# Revit family: HPLC_BARCELONA
name_source: partatom
category: Furniture
units: mm (PartAtom-declared; Revit-internal decimal feet)

## family parameters
Always vertical = Yes
Cut with Voids When Loaded = No
OmniClass Number = 23.40.20.00
OmniClass Title = General Furniture and Specialties
Room Calculation Point = No
Shared = No
Work Plane-Based = No

## types (32) — shared parameters
BS = No
BS-15 = No
BS-9 = No
BSP-15 = No
BSP-9 = No
BS_PASSTHROUGH = No
CER = No
CUTOUT_CENTER = No
CUTOUT_CENTER_CHECK = No
CUTOUT_SIDES = No
CUTOUT_SIDES_CHECK = No
FIXED = Yes
FX_MARINE_EDGE = No
HA = No
HA_MARINE_EDGE = No
LOW_TAG = Yes
MARINE_EDGE = No
Manufacturer = IBR Innovasystem
SH1-12 = No
SH1-15 = No
SH1-9 = No
SH2-12 = No
SH2-15 = No
SH2-9 = No
SHELF_LEVEL_1 = No
SHELF_LEVEL_2 = No
URL = https://ibr-innovasystem.com
WT_MATERIAL = Plástico, blanco opaco
WT_THICK = 16 mm  [stored 0.0524934 ft]
zero-valued in all types: Cost, Default Elevation

## per-type parameters (varying)
| type | COLUMN_H | Depth | Description | Length | WTheight_nominal | WTheight_real |
| HPLCB-1575718 | 1800 mm  [stored 5.90551 ft] | 750 mm  [stored 2.46063 ft] | HPLC Bench Barcelona 1500x750x750/1800, 8xElectrical Outlets (Type TBD per project) | 1500 mm  [stored 4.92126 ft] | 750 mm  [stored 2.46063 ft] | 734 mm  [stored 2.40814 ft] |
| HPLCB-1575716 | 1570 mm | 750 mm  [stored 2.46063 ft] | HPLC Bench Barcelona 1500x750x750/1570, 8xElectrical Outlets (Type TBD per project) | 1500 mm  [stored 4.92126 ft] | 750 mm  [stored 2.46063 ft] | 734 mm  [stored 2.40814 ft] |
| HPLCB-1275718 | 1800 mm  [stored 5.90551 ft] | 750 mm  [stored 2.46063 ft] | HPLC Bench Barcelona 1200x750x750/1800, 8xElectrical Outlets (Type TBD per project) | 1200 mm  [stored 3.93701 ft] | 750 mm  [stored 2.46063 ft] | 734 mm  [stored 2.40814 ft] |
| HPLCB-1275716 | 1570 mm | 750 mm  [stored 2.46063 ft] | HPLC Bench Barcelona 1200x750x750/1570, 8xElectrical Outlets (Type TBD per project) | 1200 mm  [stored 3.93701 ft] | 750 mm  [stored 2.46063 ft] | 734 mm  [stored 2.40814 ft] |
| HPLCB-0975716 | 1570 mm | 750 mm  [stored 2.46063 ft] | HPLC Bench Barcelona 900x750x750/1570, 8xElectrical Outlets (Type TBD per project) | 900 mm  [stored 2.95276 ft] | 750 mm  [stored 2.46063 ft] | 734 mm  [stored 2.40814 ft] |
| HPLCB-0975718 | 1800 mm  [stored 5.90551 ft] | 750 mm  [stored 2.46063 ft] | HPLC Bench Barcelona 900x750x750/1800, 8xElectrical Outlets (Type TBD per project) | 900 mm  [stored 2.95276 ft] | 750 mm  [stored 2.46063 ft] | 734 mm  [stored 2.40814 ft] |
| HPLCB-7575718 | 1800 mm  [stored 5.90551 ft] | 750 mm  [stored 2.46063 ft] | HPLC Bench Barcelona 750x750x750/1800, 8xElectrical Outlets (Type TBD per project) | 750 mm  [stored 2.46063 ft] | 750 mm  [stored 2.46063 ft] | 734 mm  [stored 2.40814 ft] |
| HPLCB-7575716 | 1570 mm | 750 mm  [stored 2.46063 ft] | HPLC Bench Barcelona 750x750x750/1570, 8xElectrical Outlets (Type TBD per project) | 750 mm  [stored 2.46063 ft] | 750 mm  [stored 2.46063 ft] | 734 mm  [stored 2.40814 ft] |
| HPLCB-1590718 | 1800 mm  [stored 5.90551 ft] | 900 mm  [stored 2.95276 ft] | HPLC Bench Barcelona 1500x900x750/1800, 8xElectrical Outlets (Type TBD per project) | 1500 mm  [stored 4.92126 ft] | 750 mm  [stored 2.46063 ft] | 734 mm  [stored 2.40814 ft] |
| HPLCB-1590716 | 1570 mm | 900 mm  [stored 2.95276 ft] | HPLC Bench Barcelona 1500x900x750/1570, 8xElectrical Outlets (Type TBD per project) | 1500 mm  [stored 4.92126 ft] | 750 mm  [stored 2.46063 ft] | 734 mm  [stored 2.40814 ft] |
| HPLCB-1290716 | 1570 mm | 900 mm  [stored 2.95276 ft] | HPLC Bench Barcelona 1200x900x750/1570, 8xElectrical Outlets (Type TBD per project) | 1200 mm  [stored 3.93701 ft] | 750 mm  [stored 2.46063 ft] | 734 mm  [stored 2.40814 ft] |
| HPLCB-1290718 | 1800 mm  [stored 5.90551 ft] | 900 mm  [stored 2.95276 ft] | HPLC Bench Barcelona 1200x900x750/1800, 8xElectrical Outlets (Type TBD per project) | 1200 mm  [stored 3.93701 ft] | 750 mm  [stored 2.46063 ft] | 734 mm  [stored 2.40814 ft] |
| HPLCB-0990718 | 1800 mm  [stored 5.90551 ft] | 900 mm  [stored 2.95276 ft] | HPLC Bench Barcelona 900x900x750/1800, 8xElectrical Outlets (Type TBD per project) | 900 mm  [stored 2.95276 ft] | 750 mm  [stored 2.46063 ft] | 734 mm  [stored 2.40814 ft] |
| HPLCB-0990716 | 1570 mm | 900 mm  [stored 2.95276 ft] | HPLC Bench Barcelona 900x900x750/1570, 8xElectrical Outlets (Type TBD per project) | 900 mm  [stored 2.95276 ft] | 750 mm  [stored 2.46063 ft] | 734 mm  [stored 2.40814 ft] |
| HPLCB-7590716 | 1570 mm | 900 mm  [stored 2.95276 ft] | HPLC Bench Barcelona 750x900x750/1570, 8xElectrical Outlets (Type TBD per project) | 750 mm  [stored 2.46063 ft] | 750 mm  [stored 2.46063 ft] | 734 mm  [stored 2.40814 ft] |
| HPLCB-7590718 | 1800 mm  [stored 5.90551 ft] | 900 mm  [stored 2.95276 ft] | HPLC Bench Barcelona 750x900x750/1800, 8xElectrical Outlets (Type TBD per project) | 750 mm  [stored 2.46063 ft] | 750 mm  [stored 2.46063 ft] | 734 mm  [stored 2.40814 ft] |
| HPLCB-1575618 | 1800 mm  [stored 5.90551 ft] | 750 mm  [stored 2.46063 ft] | HPLC Bench Barcelona 1500x750x650/1800, 8xElectrical Outlets (Type TBD per project) | 1500 mm  [stored 4.92126 ft] | 650 mm  [stored 2.13255 ft] | 634 mm  [stored 2.08005 ft] |
| HPLCB-1575616 | 1570 mm | 750 mm  [stored 2.46063 ft] | HPLC Bench Barcelona 1500x750x650/1570, 8xElectrical Outlets (Type TBD per project) | 1500 mm  [stored 4.92126 ft] | 650 mm  [stored 2.13255 ft] | 634 mm  [stored 2.08005 ft] |
| HPLCB-1275616 | 1570 mm | 750 mm  [stored 2.46063 ft] | HPLC Bench Barcelona 1200x750x650/1570, 8xElectrical Outlets (Type TBD per project) | 1200 mm  [stored 3.93701 ft] | 650 mm  [stored 2.13255 ft] | 634 mm  [stored 2.08005 ft] |
| HPLCB-1275618 | 1800 mm  [stored 5.90551 ft] | 750 mm  [stored 2.46063 ft] | HPLC Bench Barcelona 1200x750x650/1800, 8xElectrical Outlets (Type TBD per project) | 1200 mm  [stored 3.93701 ft] | 650 mm  [stored 2.13255 ft] | 634 mm  [stored 2.08005 ft] |
| HPLCB-0975618 | 1800 mm  [stored 5.90551 ft] | 750 mm  [stored 2.46063 ft] | HPLC Bench Barcelona 900x750x650/1800, 8xElectrical Outlets (Type TBD per project) | 900 mm  [stored 2.95276 ft] | 650 mm  [stored 2.13255 ft] | 634 mm  [stored 2.08005 ft] |
| HPLCB-0975616 | 1570 mm | 750 mm  [stored 2.46063 ft] | HPLC Bench Barcelona 900x750x650/1570, 8xElectrical Outlets (Type TBD per project) | 900 mm  [stored 2.95276 ft] | 650 mm  [stored 2.13255 ft] | 634 mm  [stored 2.08005 ft] |
| HPLCB-7575616 | 1570 mm | 750 mm  [stored 2.46063 ft] | HPLC Bench Barcelona 750x750x650/1570, 8xElectrical Outlets (Type TBD per project) | 750 mm  [stored 2.46063 ft] | 650 mm  [stored 2.13255 ft] | 634 mm  [stored 2.08005 ft] |
| HPLCB-7575618 | 1800 mm  [stored 5.90551 ft] | 750 mm  [stored 2.46063 ft] | HPLC Bench Barcelona 750x750x650/1800, 8xElectrical Outlets (Type TBD per project) | 750 mm  [stored 2.46063 ft] | 650 mm  [stored 2.13255 ft] | 634 mm  [stored 2.08005 ft] |
| HPLCB-1590618 | 1800 mm  [stored 5.90551 ft] | 900 mm  [stored 2.95276 ft] | HPLC Bench Barcelona 1500x900x650/1800, 8xElectrical Outlets (Type TBD per project) | 1500 mm  [stored 4.92126 ft] | 650 mm  [stored 2.13255 ft] | 634 mm  [stored 2.08005 ft] |
| HPLCB-1590616 | 1570 mm | 900 mm  [stored 2.95276 ft] | HPLC Bench Barcelona 1500x900x650/1570, 8xElectrical Outlets (Type TBD per project) | 1500 mm  [stored 4.92126 ft] | 650 mm  [stored 2.13255 ft] | 634 mm  [stored 2.08005 ft] |
| HPLCB-1290616 | 1570 mm | 900 mm  [stored 2.95276 ft] | HPLC Bench Barcelona 1200x900x650/1570, 8xElectrical Outlets (Type TBD per project) | 1200 mm  [stored 3.93701 ft] | 650 mm  [stored 2.13255 ft] | 634 mm  [stored 2.08005 ft] |
| HPLCB-1290618 | 1800 mm  [stored 5.90551 ft] | 900 mm  [stored 2.95276 ft] | HPLC Bench Barcelona 1200x900x650/1800, 8xElectrical Outlets (Type TBD per project) | 1200 mm  [stored 3.93701 ft] | 650 mm  [stored 2.13255 ft] | 634 mm  [stored 2.08005 ft] |
| HPLCB-0990618 | 1800 mm  [stored 5.90551 ft] | 900 mm  [stored 2.95276 ft] | HPLC Bench Barcelona 900x900x650/1800, 8xElectrical Outlets (Type TBD per project) | 900 mm  [stored 2.95276 ft] | 650 mm  [stored 2.13255 ft] | 634 mm  [stored 2.08005 ft] |
| HPLCB-0990616 | 1570 mm | 900 mm  [stored 2.95276 ft] | HPLC Bench Barcelona 900x900x650/1570, 8xElectrical Outlets (Type TBD per project) | 900 mm  [stored 2.95276 ft] | 650 mm  [stored 2.13255 ft] | 634 mm  [stored 2.08005 ft] |
| HPLCB-7590616 | 1570 mm | 900 mm  [stored 2.95276 ft] | HPLC Bench Barcelona 750x900x650/1570, 8xElectrical Outlets (Type TBD per project) | 750 mm  [stored 2.46063 ft] | 650 mm  [stored 2.13255 ft] | 634 mm  [stored 2.08005 ft] |
| HPLCB-7590618 | 1800 mm  [stored 5.90551 ft] | 900 mm  [stored 2.95276 ft] | HPLC Bench Barcelona 750x900x650/1800, 8xElectrical Outlets (Type TBD per project) | 750 mm  [stored 2.46063 ft] | 650 mm  [stored 2.13255 ft] | 634 mm  [stored 2.08005 ft] |

note: [stored X ft] marks values corroborated as IEEE doubles in the binary element streams (Revit-internal decimal feet)

## geometry (parser evidence)
native form markers: Sweep x34
no freeform markers — native parametric forms only
